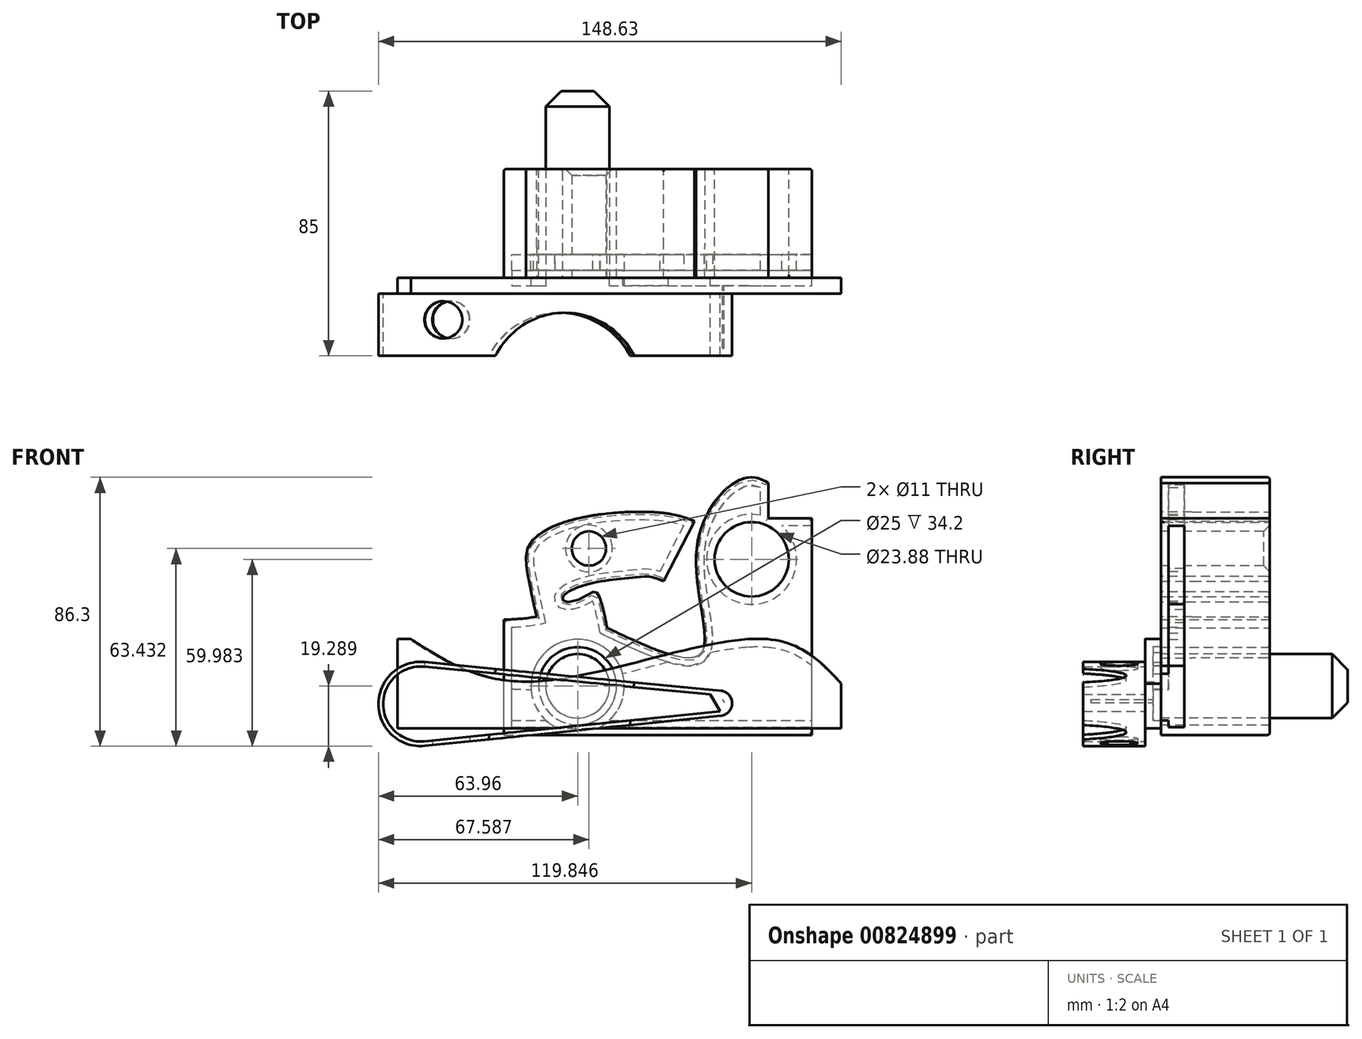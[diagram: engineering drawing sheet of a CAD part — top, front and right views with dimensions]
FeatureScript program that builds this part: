
annotation { "Feature Type Name" : "Feature", "Feature Type Description" : "" }
export const myFeature = defineFeature(function(context is Context, id is Id, definition is map)
    precondition{}
    {
        {
            var Q0;
            Q0=qCreatedBy(makeId("Front.planeOp"),FACE);
            var sketch = newSketch(context, id + "F0", { "sketchPlane" : qUnion([Q0])});
            skLineSegment(sketch, "E0.bottom", {"start": v(-49.5, -52.62) * mm, "end": v(49.5, -52.62) * mm});
            skLineSegment(sketch, "E0.left", {"start": v(-49.5, -52.62) * mm, "end": v(-49.5, -15.57) * mm});
            skLineSegment(sketch, "E0.right", {"start": v(49.5, -52.62) * mm, "end": v(49.5, 16.96) * mm});
            skArc(sketch, "E1", {"start": v(-49.5, -15.57) * mm, "mid": v(-43.6, -15.29) * mm, "end": v(-37.76, -14.45) * mm});
            skLineSegment(sketch, "E2", {"start": v(49.5, 16.96) * mm, "end": v(35.48, 16.96) * mm});
            skLineSegment(sketch, "E3", {"start": v(35.48, 16.96) * mm, "end": v(35.48, 28.22) * mm});
            skLineSegment(sketch, "E4", {"start": v(-16.33, -18.24) * mm, "end": v(-37.76, -20.8) * mm});
            skLineSegment(sketch, "E5", {"start": v(-37.76, -20.8) * mm, "end": v(-37.76, -14.45) * mm});
            skPoint(sketch, "E6.0.internal.snap0", {"position": v(35.48, 24.02) * mm});
            skFitSpline(sketch, "E6", {"points": [v(40.58, 24.02) * mm, v(28.76, 30) * mm, v(12.5, 7.7) * mm, v(13.84, -26.44) * mm, v(-16.33, -18.24) * mm], "startDerivative": vector(-61.3, 55.93) * mm, "endDerivative": vector(-144.8, 68.73) * mm});
            skPoint(sketch, "E7.orphan", {"position": v(5.1, -15.69) * mm});
            skPoint(sketch, "E8.end.orphan", {"position": v(19.89, 31.07) * mm});
            skPoint(sketch, "E9.orphan", {"position": v(35.48, 31.07) * mm});
            skCircle(sketch, "E10", {"center": v(-25.8, -36.92) * mm, "radius": 12.5 * mm});
            skCircle(sketch, "E11", {"center": v(30.09, 3.77) * mm, "radius": 11.94 * mm});
            skSolve(sketch);
        }
        {
            var Q0;
            Q0 = qSketchRegion(id + "F0", true);
            extrude(context, id + "F1", {"entities" : qUnion([Q0]), "depth" : 10 * mm, "offsetDistance" : 25 * mm});
        }
        {
            var Q0;
            Q0=makeQuery(id+"F1.opExtrude","CAP_FACE",FACE,{"disambiguationData":[OSD([sQuery(id+"F0.wireOp",EDGE,"E0.bottom"),sQuery(id+"F0.wireOp",EDGE,"E0.left"),sQuery(id+"F0.wireOp",EDGE,"E0.right"),sQuery(id+"F0.wireOp",EDGE,"E1"),sQuery(id+"F0.wireOp",EDGE,"E2"),sQuery(id+"F0.wireOp",EDGE,"E3"),sQuery(id+"F0.wireOp",EDGE,"E4"),sQuery(id+"F0.wireOp",EDGE,"E5"),sQuery(id+"F0.wireOp",EDGE,"E6"),sQuery(id+"F0.wireOp",EDGE,"E10")])],"isStart":false});
            var sketch = newSketch(context, id + "F2", { "sketchPlane" : qUnion([Q0])});
            skLineSegment(sketch, "E12.bottom", {"start": v(-83.67, -50.45) * mm, "end": v(58.87, -50.45) * mm});
            skLineSegment(sketch, "E12.top", {"start": v(-83.67, -21.86) * mm, "end": v(-79.32, -21.86) * mm});
            skLineSegment(sketch, "E12.left", {"start": v(-83.67, -50.45) * mm, "end": v(-83.67, -21.86) * mm});
            skLineSegment(sketch, "E12.right", {"start": v(58.87, -50.45) * mm, "end": v(58.87, -36.16) * mm});
            skFitSpline(sketch, "E13", {"points": [v(-79.32, -21.86) * mm, v(-40.89, -35.5) * mm, v(35.02, -21.86) * mm, v(58.87, -36.16) * mm], "startDerivative": vector(104.5, -67.37) * mm, "endDerivative": vector(71.88, -77.87) * mm});
            skLineSegment(sketch, "E14.trimOffspring", {"start": v(28.9, -21.86) * mm, "end": v(35.02, -21.86) * mm});
            skPoint(sketch, "E15.orphan", {"position": v(58.87, -21.86) * mm});
            skSolve(sketch);
        }
        {
            var Q0;
            Q0 = qSketchRegion(id + "F2", true);
            extrude(context, id + "F3", {"entities" : qUnion([Q0]), "operationType" : NewBodyOperationType.ADD, "depth" : 5 * mm, "offsetDistance" : 25 * mm});
        }
        {
            var Q0;
            Q0=makeQuery(id+"F3.opExtrude","CAP_FACE",FACE,{"disambiguationData":[OSD([sQuery(id+"F2.wireOp",EDGE,"E12.bottom"),sQuery(id+"F2.wireOp",EDGE,"E12.top"),sQuery(id+"F2.wireOp",EDGE,"E12.left"),sQuery(id+"F2.wireOp",EDGE,"E12.right"),sQuery(id+"F2.wireOp",EDGE,"E13")])],"isStart":false});
            var sketch = newSketch(context, id + "F4", { "sketchPlane" : qUnion([Q0])});
            skArc(sketch, "E16", {"start": v(-74.92, -29.21) * mm, "mid": v(-89.76, -42.7) * mm, "end": v(-74.86, -56.14) * mm});
            skArc(sketch, "E17", {"start": v(20.18, -46.48) * mm, "mid": v(23.81, -42.46) * mm, "end": v(20.17, -38.45) * mm});
            skLineSegment(sketch, "E18", {"start": v(-74.92, -29.21) * mm, "end": v(20.17, -38.45) * mm});
            skLineSegment(sketch, "E19", {"start": v(-74.86, -56.14) * mm, "end": v(20.18, -46.48) * mm});
            skLineSegment(sketch, "E20.0", {"start": v(-75.04, -30.7) * mm, "end": v(16.85, -39.63) * mm});
            skArc(sketch, "E21.0", {"start": v(-75.04, -30.7) * mm, "mid": v(-88.26, -42.7) * mm, "end": v(-75, -54.65) * mm});
            skLineSegment(sketch, "E22.0", {"start": v(-75, -54.65) * mm, "end": v(20.03, -44.99) * mm});
            skLineSegment(sketch, "E23", {"start": v(16.85, -39.63) * mm, "end": v(20.03, -44.99) * mm});
            skSolve(sketch);
        }
        {
            var Q0;
            Q0 = qSketchRegion(id + "F4", true);
            extrude(context, id + "F5", {"entities" : qUnion([Q0]), "operationType" : NewBodyOperationType.ADD, "depth" : 20 * mm, "offsetDistance" : 25 * mm});
        }
        {
            var Q0;
            Q0=makeQuery(id+"F5.opExtrude","SWEPT_FACE",FACE,{"disambiguationData":[OSD([sQuery(id+"F4.wireOp",EDGE,"E22.0")])]});
            var sketch = newSketch(context, id + "F6", { "sketchPlane" : qUnion([Q0])});
            skCircle(sketch, "E24", {"center": v(-71.58, -23.43) * mm, "radius": 6 * mm});
            skSolve(sketch);
        }
        {
            var Q0;
            Q0=makeQuery(id+"F6.imprint","IMPRINT",FACE,{"disambiguationData":[TD([[makeQuery(id+"F6.imprint","IMPRINT",EDGE,{"derivedFrom":sQuery(id+"F6.wireOp",EDGE,"E24")}),1.0]])]});
            extrude(context, id + "F7", {"entities" : qUnion([Q0]), "operationType" : NewBodyOperationType.REMOVE, "endBound" : BoundingType.SYMMETRIC, "depth" : 60 * mm, "offsetDistance" : 25 * mm});
        }
        {
            var Q0;
            Q0=makeQuery(id+"F5.opExtrude","SWEPT_FACE",FACE,{"disambiguationData":[OSD([sQuery(id+"F4.wireOp",EDGE,"E18")])]});
            var sketch = newSketch(context, id + "F8", { "sketchPlane" : qUnion([Q0])});
            skCircle(sketch, "E25", {"center": v(-26.53, -46.17) * mm, "radius": 25 * mm});
            skPoint(sketch, "E26", {"position": v(-1.53, -46.17) * mm});
            skSolve(sketch);
        }
        {
            var Q0;
            {var subQ0=sQuery(id+"F8.wireOp",EDGE,"E25");var subQ1=makeQuery(id+"F5.opExtrude","CAP_EDGE",EDGE,{"disambiguationData":[OSD([sQuery(id+"F4.wireOp",EDGE,"E18")])],"isStart":false});var subQ2=makeQuery(id+"F8.imprint","INTERSECT",VERTEX,{"disambiguationData":[OD(0.0)],"derivedFrom":[subQ1,subQ0]});Q0=makeQuery(id+"F8.imprint","IMPRINT",FACE,{"disambiguationData":[TD([[makeQuery(id+"F8.imprint","IMPRINT",EDGE,{"disambiguationData":[TD([[subQ2,-1.0]])],"derivedFrom":subQ0}),1.0]])]});}
            var Q1;
            {var subQ0=sQuery(id+"F8.wireOp",EDGE,"E25");var subQ1=makeQuery(id+"F5.opExtrude","CAP_EDGE",EDGE,{"disambiguationData":[OSD([sQuery(id+"F4.wireOp",EDGE,"E18")])],"isStart":false});var subQ2=makeQuery(id+"F8.imprint","INTERSECT",VERTEX,{"disambiguationData":[OD(0.0)],"derivedFrom":[subQ1,subQ0]});Q1=makeQuery(id+"F8.imprint","IMPRINT",FACE,{"disambiguationData":[TD([[makeQuery(id+"F8.imprint","IMPRINT",EDGE,{"disambiguationData":[TD([[subQ2,1.0]])],"derivedFrom":subQ0}),1.0]])]});}
            var Q2;
            Q2=sQuery(id+"F8.wireOp",EDGE,"E25");
            extrude(context, id + "F9", {"entities" : qUnion([Q0, Q1]), "operationType" : NewBodyOperationType.REMOVE, "surfaceEntities" : qUnion([Q2]), "oppositeDirection" : true, "depth" : 35 * mm, "offsetDistance" : 25 * mm});
        }
        {
            var Q0;
            {var subQ0=sQuery(id+"F0.wireOp",EDGE,"E5");var subQ1=sQuery(id+"F0.wireOp",EDGE,"E1");var subQ2=sQuery(id+"F0.wireOp",EDGE,"E4");var subQ3=sQuery(id+"F0.wireOp",EDGE,"E0.left");var subQ4=sQuery(id+"F0.wireOp",EDGE,"E6");var subQ5=sQuery(id+"F0.wireOp",EDGE,"E10");Q0=makeQuery(id+"F3.boolean.opBoolean","SPLIT",FACE,{"disambiguationData":[TD([makeQuery(id+"F1.opExtrude","SWEPT_FACE",FACE,{"disambiguationData":[OSD([subQ1])]})])],"derivedFrom":makeQuery(id+"F1.opExtrude","CAP_FACE",FACE,{"disambiguationData":[OSD([sQuery(id+"F0.wireOp",EDGE,"E0.bottom"),subQ3,sQuery(id+"F0.wireOp",EDGE,"E0.right"),subQ1,sQuery(id+"F0.wireOp",EDGE,"E2"),sQuery(id+"F0.wireOp",EDGE,"E3"),subQ2,subQ0,subQ4,subQ5,sQuery(id+"F0.wireOp",EDGE,"E11")])],"isStart":false})});}
            var sketch = newSketch(context, id + "F10", { "sketchPlane" : qUnion([Q0])});
            skFitSpline(sketch, "E27", {"points": [v(-43.6, -15.29) * mm, v(-41.16, 14.08) * mm, v(0, 23.14) * mm, v(19.6, 17.68) * mm], "startDerivative": vector(-18.99, 102.1) * mm, "endDerivative": vector(58.24, -25.45) * mm});
            skSolve(sketch);
        }
        {
            var Q0;
            Q0=makeQuery(id+"F1.opExtrude","SWEPT_FACE",FACE,{"disambiguationData":[OSD([sQuery(id+"F0.wireOp",EDGE,"E4")])]});
            var sketch = newSketch(context, id + "F11", { "sketchPlane" : qUnion([Q0])});
            skCircle(sketch, "E28", {"center": v(-45.04, 1.75) * mm, "radius": 2.84 * mm});
            skSolve(sketch);
        }
        {
            var Q0;
            {var subQ0=sQuery(id+"F0.wireOp",EDGE,"E4");Q0=makeQuery(id+"F11.imprint","IMPRINT",FACE,{"disambiguationData":[TD([[makeQuery(id+"F11.imprint","IMPRINT",EDGE,{"derivedFrom":makeQuery(id+"F1.opExtrude","CAP_EDGE",EDGE,{"disambiguationData":[OSD([subQ0])],"isStart":true})}),1.0]])]});}
            var Q1;
            Q1=sQuery(id+"F10.wireOp",EDGE,"E27");
            sweep(context, id + "F12", {"operationType" : NewBodyOperationType.ADD, "profiles" : qUnion([Q0]), "path" : qUnion([Q1])});
        }
        {
            var Q0;
            Q0=makeQuery(id+"F1.opExtrude","SWEPT_FACE",FACE,{"disambiguationData":[OSD([sQuery(id+"F0.wireOp",EDGE,"E0.right")])]});
            shell(context, id + "F13", {"entities" : qUnion([Q0]), "thickness" : 2.5 * mm});
        }
        {
            var Q0;
            {var subQ0=sQuery(id+"F0.wireOp",EDGE,"E4");var subQ1=sQuery(id+"F10.wireOp",EDGE,"E27");Q0=makeQuery(id+"F12.boolean.opBoolean","MERGE",FACE,{"derivedFrom":[makeQuery(id+"F1.opExtrude","CAP_FACE",FACE,{"disambiguationData":[OSD([sQuery(id+"F0.wireOp",EDGE,"E0.bottom"),sQuery(id+"F0.wireOp",EDGE,"E0.left"),sQuery(id+"F0.wireOp",EDGE,"E0.right"),sQuery(id+"F0.wireOp",EDGE,"E1"),sQuery(id+"F0.wireOp",EDGE,"E2"),sQuery(id+"F0.wireOp",EDGE,"E3"),subQ0,sQuery(id+"F0.wireOp",EDGE,"E5"),sQuery(id+"F0.wireOp",EDGE,"E6"),sQuery(id+"F0.wireOp",EDGE,"E10"),sQuery(id+"F0.wireOp",EDGE,"E11")])],"isStart":true}),makeQuery(id+"F12.opSweep","SWEPT_FACE",FACE,{"disambiguationData":[OSD([subQ0,subQ1]),TDD([subQ1,makeQuery(id+"F11.imprint","IMPRINT",EDGE,{"derivedFrom":makeQuery(id+"F1.opExtrude","CAP_EDGE",EDGE,{"disambiguationData":[OSD([subQ0])],"isStart":true})})])]})]});}
            extrude(context, id + "F14", {"entities" : qUnion([Q0]), "operationType" : NewBodyOperationType.ADD, "depth" : 25 * mm, "offsetDistance" : 25 * mm});
        }
        {
            var Q0;
            {var subQ0=sQuery(id+"F0.wireOp",EDGE,"E6");var subQ1=sQuery(id+"F0.wireOp",EDGE,"E3");var subQ3=sQuery(id+"F0.wireOp",EDGE,"E2");var subQ4=sQuery(id+"F0.wireOp",EDGE,"E0.right");var subQ5=sQuery(id+"F0.wireOp",EDGE,"E11");Q0=makeQuery(id+"F3.boolean.opBoolean","SPLIT",FACE,{"disambiguationData":[TD([makeQuery(id+"F1.opExtrude","SWEPT_FACE",FACE,{"disambiguationData":[OSD([subQ3])]})])],"derivedFrom":makeQuery(id+"F1.opExtrude","CAP_FACE",FACE,{"disambiguationData":[OSD([sQuery(id+"F0.wireOp",EDGE,"E0.bottom"),sQuery(id+"F0.wireOp",EDGE,"E0.left"),subQ4,sQuery(id+"F0.wireOp",EDGE,"E1"),subQ3,subQ1,sQuery(id+"F0.wireOp",EDGE,"E4"),sQuery(id+"F0.wireOp",EDGE,"E5"),subQ0,sQuery(id+"F0.wireOp",EDGE,"E10"),subQ5])],"isStart":false})});}
            var sketch = newSketch(context, id + "F15", { "sketchPlane" : qUnion([Q0])});
            skCircle(sketch, "E29", {"center": v(-25.8, -36.92) * mm, "radius": 10.26 * mm});
            skSolve(sketch);
        }
        {
            var Q0;
            Q0=makeQuery(id+"F15.imprint","IMPRINT",FACE,{"disambiguationData":[TD([[makeQuery(id+"F15.imprint","IMPRINT",EDGE,{"derivedFrom":sQuery(id+"F15.wireOp",EDGE,"E29")}),1.0]])]});
            var Q1;
            Q1=sQuery(id+"F15.wireOp",EDGE,"E29");
            extrude(context, id + "F16", {"entities" : qUnion([Q0]), "operationType" : NewBodyOperationType.ADD, "surfaceEntities" : qUnion([Q1]), "oppositeDirection" : true, "depth" : 60 * mm, "offsetDistance" : 25 * mm});
        }
        {
            var Q0;
            {var subQ0=sQuery(id+"F0.wireOp",EDGE,"E6");var subQ1=sQuery(id+"F0.wireOp",EDGE,"E3");var subQ3=sQuery(id+"F0.wireOp",EDGE,"E2");var subQ4=sQuery(id+"F0.wireOp",EDGE,"E0.right");var subQ5=sQuery(id+"F0.wireOp",EDGE,"E11");Q0=makeQuery(id+"F3.boolean.opBoolean","SPLIT",FACE,{"disambiguationData":[TD([makeQuery(id+"F1.opExtrude","SWEPT_FACE",FACE,{"disambiguationData":[OSD([subQ3])]})])],"derivedFrom":makeQuery(id+"F1.opExtrude","CAP_FACE",FACE,{"disambiguationData":[OSD([sQuery(id+"F0.wireOp",EDGE,"E0.bottom"),sQuery(id+"F0.wireOp",EDGE,"E0.left"),subQ4,sQuery(id+"F0.wireOp",EDGE,"E1"),subQ3,subQ1,sQuery(id+"F0.wireOp",EDGE,"E4"),sQuery(id+"F0.wireOp",EDGE,"E5"),subQ0,sQuery(id+"F0.wireOp",EDGE,"E10"),subQ5])],"isStart":false})});}
            var sketch = newSketch(context, id + "F17", { "sketchPlane" : qUnion([Q0])});
            skCircle(sketch, "E30", {"center": v(30.09, 3.77) * mm, "radius": 10.67 * mm});
            skSolve(sketch);
        }
        {
            var Q0;
            Q0=makeQuery(id+"F17.imprint","IMPRINT",FACE,{"disambiguationData":[TD([[makeQuery(id+"F17.imprint","IMPRINT",EDGE,{"derivedFrom":sQuery(id+"F17.wireOp",EDGE,"E30")}),1.0]])]});
            var Q1;
            Q1=sQuery(id+"F17.wireOp",EDGE,"E30");
            extrude(context, id + "F18", {"entities" : qUnion([Q0]), "operationType" : NewBodyOperationType.ADD, "surfaceEntities" : qUnion([Q1]), "depth" : 25 * mm, "offsetDistance" : 25 * mm});
        }
        {
            var Q0;
            Q0=makeQuery(id+"F18.opExtrude","CAP_FACE",FACE,{"disambiguationData":[OSD([sQuery(id+"F17.wireOp",EDGE,"E30")])],"isStart":false});
            shell(context, id + "F19", {"entities" : qUnion([Q0]), "thickness" : 1.5 * mm, "oppositeDirection" : true});
        }
        {
            var Q0;
            Q0=makeQuery(id+"F16.opExtrude","CAP_FACE",FACE,{"disambiguationData":[OSD([sQuery(id+"F15.wireOp",EDGE,"E29")])],"isStart":false});
            chamfer(context, id + "F20", {"entities" : qUnion([Q0]), "width" : 5 * mm, "tangentPropagation" : true});
        }
        {
            var Q0;
            {var subQ0=sQuery(id+"F0.wireOp",EDGE,"E11");Q0=makeQuery(id+"F14.boolean.opBoolean","MERGE",FACE,{"derivedFrom":[makeQuery(id+"F1.opExtrude","SWEPT_FACE",FACE,{"disambiguationData":[OSD([subQ0])]}),makeQuery(id+"F14.opExtrude","SWEPT_FACE",FACE,{"disambiguationData":[OSD([subQ0])]})]});}
            fillet(context, id + "F21", {"entities" : qUnion([Q0]), "radius" : 1 * mm, "tangentPropagation" : true, "allowEdgeOverflow" : false});
        }
        {
            var Q0;
            Q0=makeQuery(id+"F14.opExtrude","CAP_FACE",FACE,{"disambiguationData":[OSD([sQuery(id+"F0.wireOp",EDGE,"E0.bottom"),sQuery(id+"F0.wireOp",EDGE,"E0.left"),sQuery(id+"F0.wireOp",EDGE,"E0.right"),sQuery(id+"F0.wireOp",EDGE,"E1"),sQuery(id+"F0.wireOp",EDGE,"E2"),sQuery(id+"F0.wireOp",EDGE,"E3"),sQuery(id+"F0.wireOp",EDGE,"E4"),sQuery(id+"F0.wireOp",EDGE,"E5"),sQuery(id+"F0.wireOp",EDGE,"E6"),sQuery(id+"F0.wireOp",EDGE,"E10"),sQuery(id+"F0.wireOp",EDGE,"E11"),sQuery(id+"F10.wireOp",EDGE,"E27")])],"isStart":false});
            var Q1;
            Q1=makeQuery(id+"F16.opExtrude","CAP_FACE",FACE,{"disambiguationData":[OSD([sQuery(id+"F15.wireOp",EDGE,"E29")])],"isStart":false});
            fillet(context, id + "F22", {"entities" : qUnion([Q0, Q1]), "radius" : 0.8 * mm, "tangentPropagation" : true, "allowEdgeOverflow" : false});
        }
        {
            var Q0;
            Q0=makeQuery(id+"F18.opExtrude","SWEPT_BODY",BODY,{"disambiguationData":[OSD([sQuery(id+"F17.wireOp",EDGE,"E30")])]});
            deleteBodies(context, id + "F23", {"entities" : qUnion([Q0])});
        }
        {
            var Q0;
            {var subQ0=sQuery(id+"F0.wireOp",EDGE,"E4");var subQ1=sQuery(id+"F10.wireOp",EDGE,"E27");var subQ2=sQuery(id+"F0.wireOp",EDGE,"E5");var subQ3=sQuery(id+"F0.wireOp",EDGE,"E1");var subQ4=sQuery(id+"F0.wireOp",EDGE,"E0.left");var subQ5=sQuery(id+"F0.wireOp",EDGE,"E6");var subQ6=sQuery(id+"F0.wireOp",EDGE,"E10");Q0=makeQuery(id+"F12.boolean.opBoolean","MERGE",FACE,{"derivedFrom":[makeQuery(id+"F3.boolean.opBoolean","SPLIT",FACE,{"disambiguationData":[TD([makeQuery(id+"F1.opExtrude","SWEPT_FACE",FACE,{"disambiguationData":[OSD([subQ3])]})])],"derivedFrom":makeQuery(id+"F1.opExtrude","CAP_FACE",FACE,{"disambiguationData":[OSD([sQuery(id+"F0.wireOp",EDGE,"E0.bottom"),subQ4,sQuery(id+"F0.wireOp",EDGE,"E0.right"),subQ3,sQuery(id+"F0.wireOp",EDGE,"E2"),sQuery(id+"F0.wireOp",EDGE,"E3"),subQ0,subQ2,subQ5,subQ6,sQuery(id+"F0.wireOp",EDGE,"E11")])],"isStart":false})}),makeQuery(id+"F12.opSweep","SWEPT_FACE",FACE,{"disambiguationData":[OSD([subQ0,subQ1]),TDD([subQ1,makeQuery(id+"F11.imprint","IMPRINT",EDGE,{"derivedFrom":makeQuery(id+"F1.opExtrude","CAP_EDGE",EDGE,{"disambiguationData":[OSD([subQ0])],"isStart":false})})])]})]});}
            var sketch = newSketch(context, id + "F24", { "sketchPlane" : qUnion([Q0])});
            skCircle(sketch, "E31", {"center": v(-22.17, 7.22) * mm, "radius": 5.5 * mm});
            skSolve(sketch);
        }
        {
            var Q0;
            Q0 = qSketchRegion(id + "F24", true);
            extrude(context, id + "F25", {"entities" : qUnion([Q0]), "operationType" : NewBodyOperationType.REMOVE, "oppositeDirection" : true, "depth" : 50 * mm, "offsetDistance" : 25 * mm});
        }
        {
            var Q0;
            Q0=makeQuery(id+"F25.boolean.opBoolean","INTERSECT",EDGE,{"derivedFrom":[makeQuery(id+"F14.opExtrude","CAP_FACE",FACE,{"disambiguationData":[OSD([sQuery(id+"F0.wireOp",EDGE,"E0.bottom"),sQuery(id+"F0.wireOp",EDGE,"E0.left"),sQuery(id+"F0.wireOp",EDGE,"E0.right"),sQuery(id+"F0.wireOp",EDGE,"E1"),sQuery(id+"F0.wireOp",EDGE,"E2"),sQuery(id+"F0.wireOp",EDGE,"E3"),sQuery(id+"F0.wireOp",EDGE,"E4"),sQuery(id+"F0.wireOp",EDGE,"E5"),sQuery(id+"F0.wireOp",EDGE,"E6"),sQuery(id+"F0.wireOp",EDGE,"E10"),sQuery(id+"F0.wireOp",EDGE,"E11"),sQuery(id+"F10.wireOp",EDGE,"E27")])],"isStart":false}),makeQuery(id+"F25.opExtrude","SWEPT_FACE",FACE,{"disambiguationData":[OSD([sQuery(id+"F24.wireOp",EDGE,"E31")])]})]});
            var Q1;
            Q1=makeQuery(id+"F25.boolean.opBoolean","COPY",EDGE,{"derivedFrom":makeQuery(id+"F25.opExtrude","CAP_EDGE",EDGE,{"disambiguationData":[OSD([sQuery(id+"F24.wireOp",EDGE,"E31")])],"isStart":true})});
            chamfer(context, id + "F26", {"entities" : qUnion([Q0, Q1]), "width" : 2 * mm});
        }
    });
